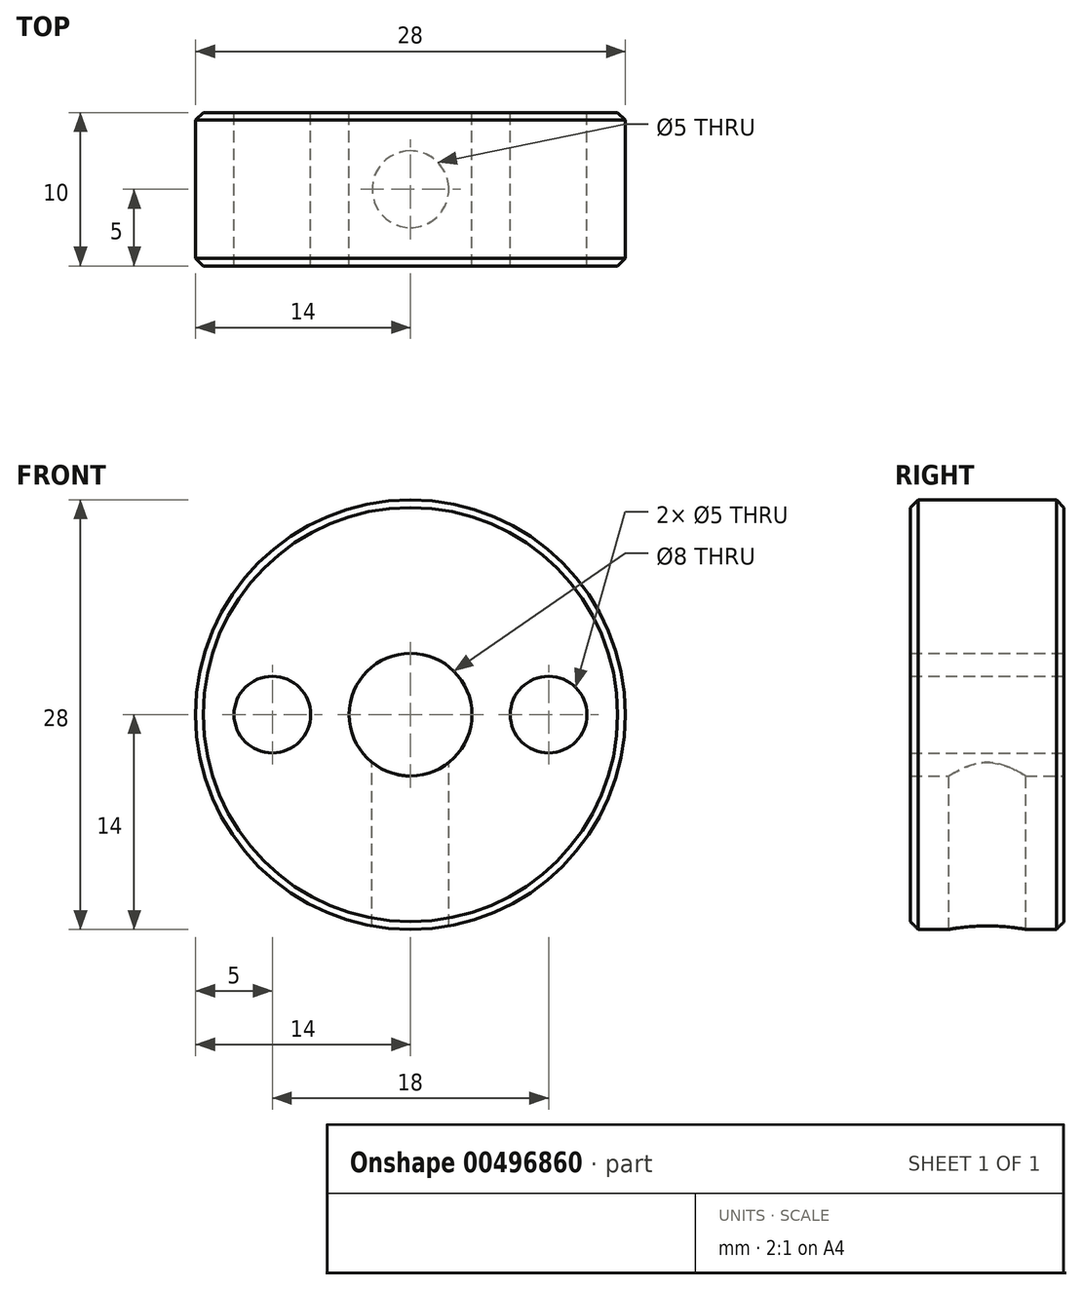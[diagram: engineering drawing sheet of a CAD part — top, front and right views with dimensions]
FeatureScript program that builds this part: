
annotation { "Feature Type Name" : "Feature", "Feature Type Description" : "" }
export const myFeature = defineFeature(function(context is Context, id is Id, definition is map)
    precondition{}
    {
        {
            var Q0;
            Q0=qCreatedBy(makeId("Front.planeOp"),FACE);
            var sketch = newSketch(context, id + "F0", { "sketchPlane" : qUnion([Q0])});
            skCircle(sketch, "E0", {"center": v(0, 0) * mm, "radius": 4 * mm});
            skCircle(sketch, "E1", {"center": v(0, 0) * mm, "radius": 14 * mm});
            skLineSegment(sketch, "E2", {"start": v(0, 0) * mm, "end": v(-9, 0) * mm});
            skLineSegment(sketch, "E3", {"start": v(0, 0) * mm, "end": v(9, 0) * mm});
            skCircle(sketch, "E4", {"center": v(-9, 0) * mm, "radius": 2.5 * mm});
            skCircle(sketch, "E5", {"center": v(9, 0) * mm, "radius": 2.5 * mm});
            skSolve(sketch);
        }
        {
            var Q0;
            Q0 = qSketchRegion(id + "F0", true);
            extrude(context, id + "F1", {"entities" : qUnion([Q0]), "depth" : 10 * mm});
        }
        {
            var Q0;
            Q0=makeQuery(id+"F1.opExtrude","CAP_EDGE",EDGE,{"disambiguationData":[OSD([sQuery(id+"F0.wireOp",EDGE,"E1")])],"isStart":false});
            var Q1;
            Q1=makeQuery(id+"F1.opExtrude","CAP_EDGE",EDGE,{"disambiguationData":[OSD([sQuery(id+"F0.wireOp",EDGE,"E1")])],"isStart":true});
            chamfer(context, id + "F2", {"entities" : qUnion([Q0, Q1]), "width" : 0.5 * mm, "tangentPropagation" : true});
        }
        {
            var Q0;
            Q0=qCreatedBy(makeId("Top.planeOp"),FACE);
            var sketch = newSketch(context, id + "F3", { "sketchPlane" : qUnion([Q0])});
            skCircle(sketch, "E6", {"center": v(0, -5) * mm, "radius": 2.5 * mm});
            skSolve(sketch);
        }
        {
            var Q0;
            Q0 = qSketchRegion(id + "F3", true);
            extrude(context, id + "F4", {"entities" : qUnion([Q0]), "operationType" : NewBodyOperationType.REMOVE, "oppositeDirection" : true, "depth" : 25 * mm});
        }
    });
